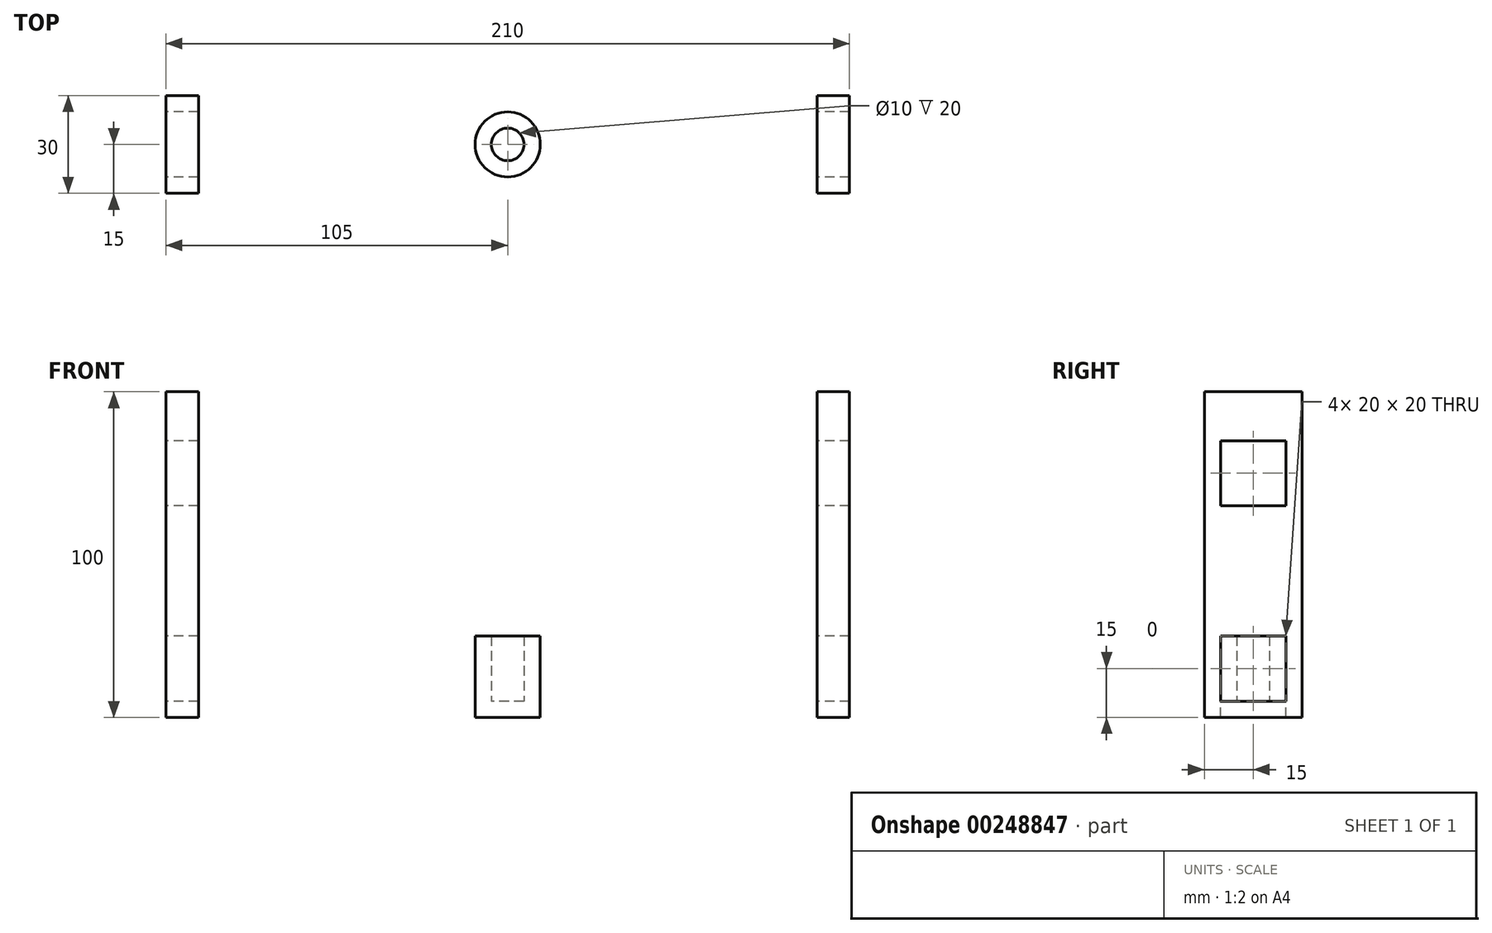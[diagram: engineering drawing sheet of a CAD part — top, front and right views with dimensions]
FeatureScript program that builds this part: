
annotation { "Feature Type Name" : "Feature", "Feature Type Description" : "" }
export const myFeature = defineFeature(function(context is Context, id is Id, definition is map)
    precondition{}
    {
        {
            var Q0;
            Q0=qCreatedBy(makeId("Top.planeOp"),FACE);
            var sketch = newSketch(context, id + "F0", { "sketchPlane" : qUnion([Q0])});
            skCircle(sketch, "E0", {"center": v(0, 0) * mm, "radius": 10 * mm});
            skCircle(sketch, "E1", {"center": v(0, 0) * mm, "radius": 5 * mm});
            skLineSegment(sketch, "E2.bottom", {"start": v(95, 15) * mm, "end": v(105, 15) * mm});
            skLineSegment(sketch, "E2.top", {"start": v(95, -15) * mm, "end": v(105, -15) * mm});
            skLineSegment(sketch, "E2.left", {"start": v(95, 15) * mm, "end": v(95, -15) * mm});
            skLineSegment(sketch, "E2.right", {"start": v(105, 15) * mm, "end": v(105, -15) * mm});
            skPoint(sketch, "E2.middle", {"position": v(100, 0) * mm});
            skLineSegment(sketch, "E3.bottom", {"start": v(-105, 15) * mm, "end": v(-95, 15) * mm});
            skLineSegment(sketch, "E3.top", {"start": v(-105, -15) * mm, "end": v(-95, -15) * mm});
            skLineSegment(sketch, "E3.left", {"start": v(-105, 15) * mm, "end": v(-105, -15) * mm});
            skLineSegment(sketch, "E3.right", {"start": v(-95, 15) * mm, "end": v(-95, -15) * mm});
            skPoint(sketch, "E3.middle", {"position": v(-100, 0) * mm});
            skLineSegment(sketch, "E4", {"start": v(-95, 10) * mm, "end": v(95, 10) * mm});
            skPoint(sketch, "E4.endSnap0", {"position": v(95, 0) * mm});
            skLineSegment(sketch, "E5", {"start": v(95, 10) * mm, "end": v(95, -10) * mm});
            skLineSegment(sketch, "E6", {"start": v(-95, -10) * mm, "end": v(-95, 10) * mm});
            skLineSegment(sketch, "E7", {"start": v(-95, -10) * mm, "end": v(95, -10) * mm});
            skSolve(sketch);
        }
        {
            var Q0;
            Q0=qCreatedBy(makeId("Right.planeOp"),FACE);
            var sketch = newSketch(context, id + "F1", { "sketchPlane" : qUnion([Q0])});
            skLineSegment(sketch, "E8.bottom", {"start": v(-10, 0) * mm, "end": v(10, 0) * mm});
            skLineSegment(sketch, "E8.top", {"start": v(-10, 20) * mm, "end": v(10, 20) * mm});
            skLineSegment(sketch, "E8.left", {"start": v(-10, 0) * mm, "end": v(-10, 20) * mm});
            skLineSegment(sketch, "E8.right", {"start": v(10, 0) * mm, "end": v(10, 20) * mm});
            skPoint(sketch, "E8.middle", {"position": v(0, 10) * mm});
            skLineSegment(sketch, "E9.bottom", {"start": v(-10, 60) * mm, "end": v(10, 60) * mm});
            skLineSegment(sketch, "E9.top", {"start": v(-10, 80) * mm, "end": v(10, 80) * mm});
            skLineSegment(sketch, "E9.left", {"start": v(-10, 60) * mm, "end": v(-10, 80) * mm});
            skLineSegment(sketch, "E9.right", {"start": v(10, 60) * mm, "end": v(10, 80) * mm});
            skPoint(sketch, "E9.middle", {"position": v(0, 70) * mm});
            skSolve(sketch);
        }
        {
            var Q0;
            {var subQ1=sQuery(id+"F0.wireOp",EDGE,"E3.bottom");Q0=makeQuery(id+"F0.imprint","IMPRINT",FACE,{"disambiguationData":[TD([[makeQuery(id+"F0.imprint","IMPRINT",EDGE,{"derivedFrom":subQ1}),-1.0]])]});}
            var Q1;
            {var subQ5=sQuery(id+"F0.wireOp",EDGE,"E6");Q1=makeQuery(id+"F0.imprint","IMPRINT",FACE,{"disambiguationData":[TD([[makeQuery(id+"F0.imprint","IMPRINT",EDGE,{"derivedFrom":subQ5}),-1.0]])]});}
            var Q2;
            {var subQ5=sQuery(id+"F0.wireOp",EDGE,"E5");Q2=makeQuery(id+"F0.imprint","IMPRINT",FACE,{"disambiguationData":[TD([[makeQuery(id+"F0.imprint","IMPRINT",EDGE,{"derivedFrom":subQ5}),-1.0]])]});}
            var Q3;
            {var subQ3=sQuery(id+"F0.wireOp",EDGE,"E2.bottom");Q3=makeQuery(id+"F0.imprint","IMPRINT",FACE,{"disambiguationData":[TD([[makeQuery(id+"F0.imprint","IMPRINT",EDGE,{"derivedFrom":subQ3}),-1.0]])]});}
            var Q4;
            Q4=makeQuery(id+"F0.imprint","IMPRINT",FACE,{"disambiguationData":[TD([[makeQuery(id+"F0.imprint","IMPRINT",EDGE,{"derivedFrom":sQuery(id+"F0.wireOp",EDGE,"E1")}),-1.0]])]});
            var Q5;
            Q5=makeQuery(id+"F0.imprint","IMPRINT",FACE,{"disambiguationData":[TD([[makeQuery(id+"F0.imprint","IMPRINT",EDGE,{"derivedFrom":sQuery(id+"F0.wireOp",EDGE,"E1")}),1.0]])]});
            extrude(context, id + "F2", {"entities" : qUnion([Q0, Q1, Q2, Q3, Q4, Q5]), "oppositeDirection" : true, "depth" : 5 * mm});
        }
        {
            var Q0;
            {var subQ1=sQuery(id+"F0.wireOp",EDGE,"E3.bottom");Q0=makeQuery(id+"F0.imprint","IMPRINT",FACE,{"disambiguationData":[TD([[makeQuery(id+"F0.imprint","IMPRINT",EDGE,{"derivedFrom":subQ1}),-1.0]])]});}
            var Q1;
            {var subQ3=sQuery(id+"F0.wireOp",EDGE,"E2.bottom");Q1=makeQuery(id+"F0.imprint","IMPRINT",FACE,{"disambiguationData":[TD([[makeQuery(id+"F0.imprint","IMPRINT",EDGE,{"derivedFrom":subQ3}),-1.0]])]});}
            extrude(context, id + "F3", {"entities" : qUnion([Q0, Q1]), "operationType" : NewBodyOperationType.ADD, "depth" : 95 * mm});
        }
        {
            var Q0;
            Q0=makeQuery(id+"F1.imprint","IMPRINT",FACE,{"disambiguationData":[TD([[makeQuery(id+"F1.imprint","IMPRINT",EDGE,{"derivedFrom":sQuery(id+"F1.wireOp",EDGE,"E8.bottom")}),1.0]])]});
            var Q1;
            Q1=makeQuery(id+"F1.imprint","IMPRINT",FACE,{"disambiguationData":[TD([[makeQuery(id+"F1.imprint","IMPRINT",EDGE,{"derivedFrom":sQuery(id+"F1.wireOp",EDGE,"E9.bottom")}),1.0]])]});
            extrude(context, id + "F4", {"entities" : qUnion([Q0, Q1]), "operationType" : NewBodyOperationType.REMOVE, "endBound" : BoundingType.SYMMETRIC, "depth" : 400 * mm});
        }
        {
            var Q0;
            Q0=makeQuery(id+"F0.imprint","IMPRINT",FACE,{"disambiguationData":[TD([[makeQuery(id+"F0.imprint","IMPRINT",EDGE,{"derivedFrom":sQuery(id+"F0.wireOp",EDGE,"E1")}),-1.0]])]});
            extrude(context, id + "F5", {"entities" : qUnion([Q0]), "operationType" : NewBodyOperationType.ADD, "depth" : 20 * mm});
        }
    });
